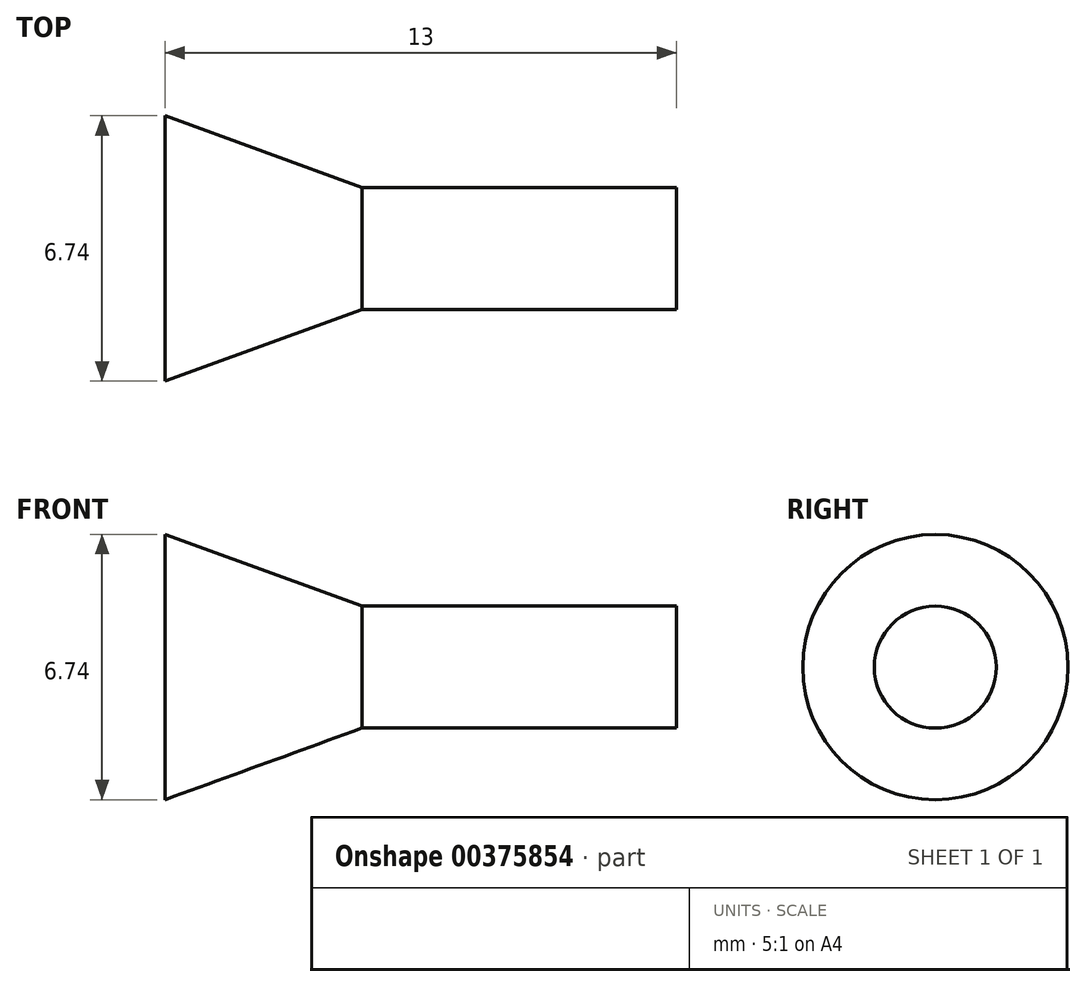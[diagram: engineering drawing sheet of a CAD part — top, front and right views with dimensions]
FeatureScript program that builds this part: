
annotation { "Feature Type Name" : "Feature", "Feature Type Description" : "" }
export const myFeature = defineFeature(function(context is Context, id is Id, definition is map)
    precondition{}
    {
        {
            var Q0;
            Q0=qCreatedBy(makeId("Right.planeOp"),FACE);
            var sketch = newSketch(context, id + "F0", { "sketchPlane" : qUnion([Q0])});
            skCircle(sketch, "E0", {"center": v(0, 0) * mm, "radius": 1.55 * mm});
            skSolve(sketch);
        }
        {
            var Q0;
            Q0 = qSketchRegion(id + "F0", true);
            extrude(context, id + "F1", {"entities" : qUnion([Q0]), "depth" : 8 * mm});
        }
        {
            var Q0;
            Q0=qCreatedBy(makeId("Right.planeOp"),FACE);
            cPlane(context, id + "F2", {"entities" : qUnion([Q0]), "cplaneType" : CPlaneType.OFFSET, "offset" : 5 * mm, "oppositeDirection" : true, "width" : 152.4 * mm, "height" : 152.4 * mm});
        }
        {
            var Q0;
            Q0=makeQuery(id+"F1.opExtrude","CAP_FACE",FACE,{"disambiguationData":[OSD([sQuery(id+"F0.wireOp",EDGE,"E0")])],"isStart":true});
            var Q1;
            Q1=qCreatedBy(id+"F2.planeOp",FACE);
            var Q2;
            Q2=makeQuery(id+"F1.opExtrude","SWEPT_BODY",BODY,{"disambiguationData":[OSD([sQuery(id+"F0.wireOp",EDGE,"E0")])]});
            extrude(context, id + "F3", {"entities" : qUnion([Q0]), "operationType" : NewBodyOperationType.ADD, "endBound" : BoundingType.UP_TO_SURFACE, "endBoundEntityFace" : qUnion([Q1]), "endBoundEntityBody" : qUnion([Q2]), "depth" : 25.4 * mm, "hasDraft" : true, "draftAngle" : 20 * degree});
        }
    });
